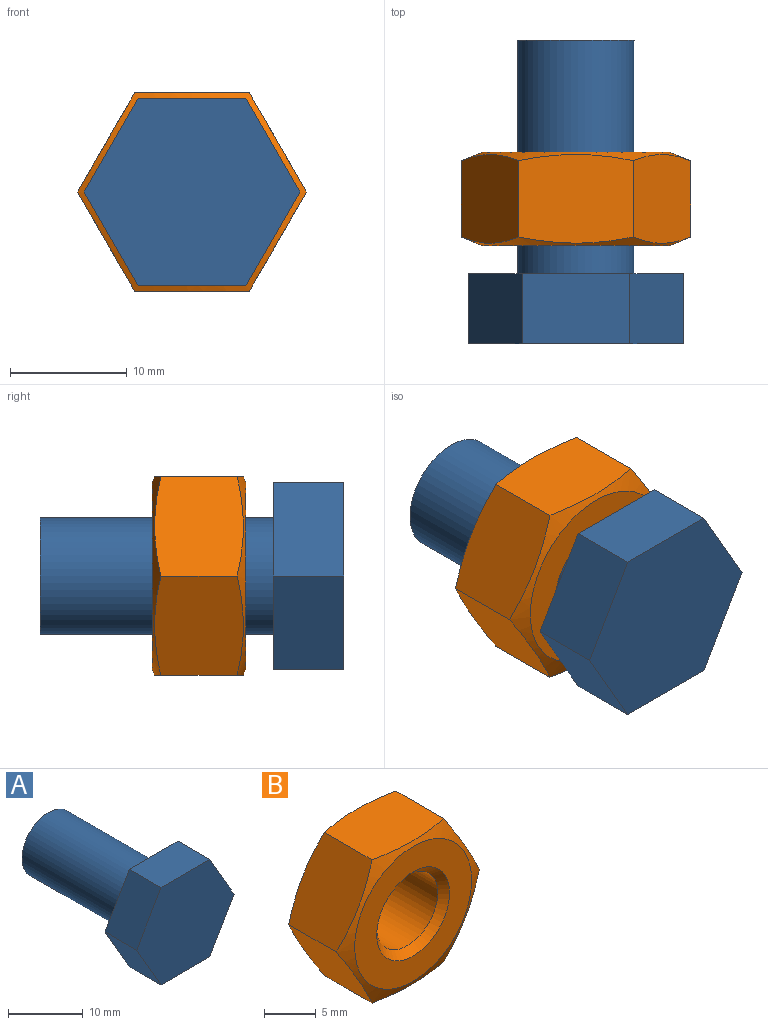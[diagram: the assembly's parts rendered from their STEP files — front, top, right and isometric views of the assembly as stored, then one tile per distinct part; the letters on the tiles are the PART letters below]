
ASSEMBLY  parts=2 mates=1
PART A: 10 faces, bbox 18.5x26x16 mm
  f0: plane 8x6mm, normal (-0.87,0,0.5), area 55.4mm2, adj f1,f5,f6,f7
  f1: plane 8x6mm, normal (-0.87,0,-0.5), area 55.4mm2, adj f0,f2,f6,f7
  f2: plane 9.24x6mm, normal (0,0,-1), area 55.4mm2, adj f1,f3,f6,f7
  f3: plane 8x6mm, normal (0.87,0,-0.5), area 55.4mm2, adj f2,f4,f6,f7
  f4: plane 8x6mm, normal (0.87,0,0.5), area 55.4mm2, adj f3,f5,f6,f7
  f5: plane 9.24x6mm, normal (0,0,1), area 55.4mm2, adj f0,f4,f6,f7
  f6: plane 18.48x16mm, normal (0,-1,0), area 221.7mm2, adj f0,f1,f2,f3,f4,f5
  f7: plane 18.48x16mm, normal (0,1,0), area 143.2mm2, adj f0,f1,f2,f3,f4,f5,f8
  f8: cylinder r=5mm len=20mm, axis (0,-1,0), area 628.3mm2, adj f7,f9
  f9: plane 10x10mm, normal (0,1,0), area 78.5mm2, adj f8
PART B: 13 faces, bbox 19.6x8x19.6 mm
  f0: cone r=8.01mm half-angle=68deg, axis (0,-1,0), area 52.3mm2, adj f1,f7,f8,f9,f10,f11,f12
  f1: plane 16.03x16.03mm, normal (0,1,0), area 123.3mm2, adj f0,f4
  f2: cone r=5mm half-angle=45deg, axis (0,-1,0), area 33.1mm2, adj f3,f5
  f3: cylinder r=4.19mm len=8.38mm, axis (0,1,0), area 167.8mm2, adj f2,f4
  f4: cone r=4.19mm half-angle=45deg, axis (0,1,0), area 33.1mm2, adj f1,f3
  f5: plane 16.03x16.03mm, normal (0,-1,0), area 123.3mm2, adj f2,f6
  f6: cone r=9.81mm half-angle=68deg, axis (0,1,0), area 52.3mm2, adj f5,f7,f8,f9,f10,f11,f12
  f7: plane 8.5x7.61mm, normal (0.87,0,-0.5), area 71.1mm2, adj f0,f6,f8,f12
  f8: plane 8.5x7.61mm, normal (0.87,0,0.5), area 71.1mm2, adj f0,f6,f7,f9
  f9: plane 9.82x7.61mm, normal (0,0,1), area 71.1mm2, adj f0,f6,f8,f10
  f10: plane 8.5x7.61mm, normal (-0.87,0,0.5), area 71.1mm2, adj f0,f6,f9,f11
  f11: plane 8.5x7.61mm, normal (-0.87,0,-0.5), area 71.1mm2, adj f0,f6,f10,f12
  f12: plane 9.82x7.61mm, normal (0,0,-1), area 71.1mm2, adj f0,f6,f7,f11
PLACE A t=(-5.97,-20.43,-22.9)mm
PLACE B t=(-63.83,-10.03,35.12)mm
MATE fastened B.f4 <-> A.f8  axis (0,-1,0) through (-63.83,-18.03,35.12)mm
